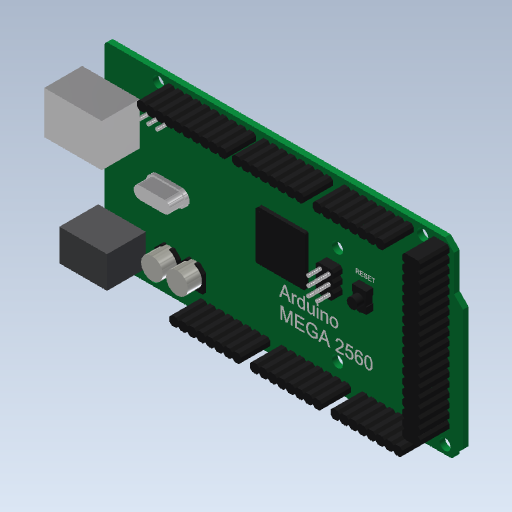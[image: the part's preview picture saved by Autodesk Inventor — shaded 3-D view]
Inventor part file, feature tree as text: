
AUTODESK INVENTOR PART (.ipt)
format: ipt  version: 2020 (Build 240168000, 168)  size: 1,370,624 bytes
history: native  units: mm (DEFAULTED — no unit token found)
features: extrude x16, sketch x8, plane x1
ambient origin geometry x8: Origin, YZ Plane, XZ Plane, XY Plane, X Axis, Y Axis, Z Axis, Center Point
bodies: Solid1 (feature_tree)
feature tree (25):
  extrude  "PCB"  Depth=53.339919mm
  sketch  "Sketch3"  dims[d53=101.599932mm d54=1.6mm d55=0.0mm]
  extrude  "Socket"  Depth=1.6mm TaperAngle=0.0deg
  extrude  "Atmel2560"  Depth=15.240007mm
  extrude  "Quarz1"  Depth=90.169956mm
  extrude  "Quarz2"  Depth=2.539965mm
  extrude  "Extrusion7"  Depth=7.619995mm
  extrude  "Extrusion8"  Depth=98.059928mm
  extrude  "Switch1"  TaperAngle=45.0deg  [1 undecoded]
  extrude  "Switch2"  Depth=5.0mm
  extrude  "Pins1"  Depth=5.0mm
  extrude  "Pins2"  Depth=5.0mm
  extrude  "Power"  Depth=5.0mm
  extrude  "Power2"  Depth=8.3mm TaperAngle=0.0deg
  extrude  "Text"  Depth=5.0mm TaperAngle=0.0deg
  plane  "Work Plane1"
  extrude  "Extrusion15"  Depth=1.0mm TaperAngle=0.0deg
  extrude  "Extrusion16"  Depth=1.0mm TaperAngle=0.0deg
  sketch  "Sketch1"  dims[d51=3.199998mm d52=53.339919mm]
  sketch  "Sketch4"  dims[d56=13.970007mm d57=15.240007mm]
  sketch  "Sketch5"  dims[d58=66.039973mm d59=90.169956mm]
  sketch  "Sketch6"  dims[d60=96.519952mm d61=2.539965mm]
  sketch  "Sketch7"  dims[d62=50.799932mm d63=7.619995mm]
  sketch  "Sketch8"  dims[d64=27.939948mm d65=98.059928mm]
  sketch  "Sketch9"  dims[d66=1.0mm d67=45.0deg d68=2.539987mm d69=2.540017mm d73=1.269977mm d74=12.699981mm d77=8.3mm d78=0.0mm d79=2.5mm d80=0.0mm d81=1.0mm d82=0.0mm d83=1.0mm d84=0.0mm d85=5.0mm d86=0.0mm d87=5.0mm d88=0.0mm d89=1.0mm d90=0.0mm d91=2.0mm d92=0.0mm d93=4.0mm d94=0.0mm d95=1.0mm d96=1.0mm d97=2.5mm d98=1.29mm d99=1.29mm d100=2.5mm d101=1.29mm d102=3.5mm d103=0.0mm d104=13.5mm d105=9.0mm d106=3.3mm d107=1.8mm d108=11.0mm d109=0.0mm d110=5.0mm d111=10.0mm d112=0.0mm d113=19.0mm d114=52.0mm d115=0.1mm d116=0.0mm d117=16.3mm d118=0.0mm d119=5.0mm d120=0.0mm]
note: 1 required parameter value undecoded (feature->parameter linkage not recoverable at this tier; creation-order binding heuristic only, values carry confidence <= 0.55)
